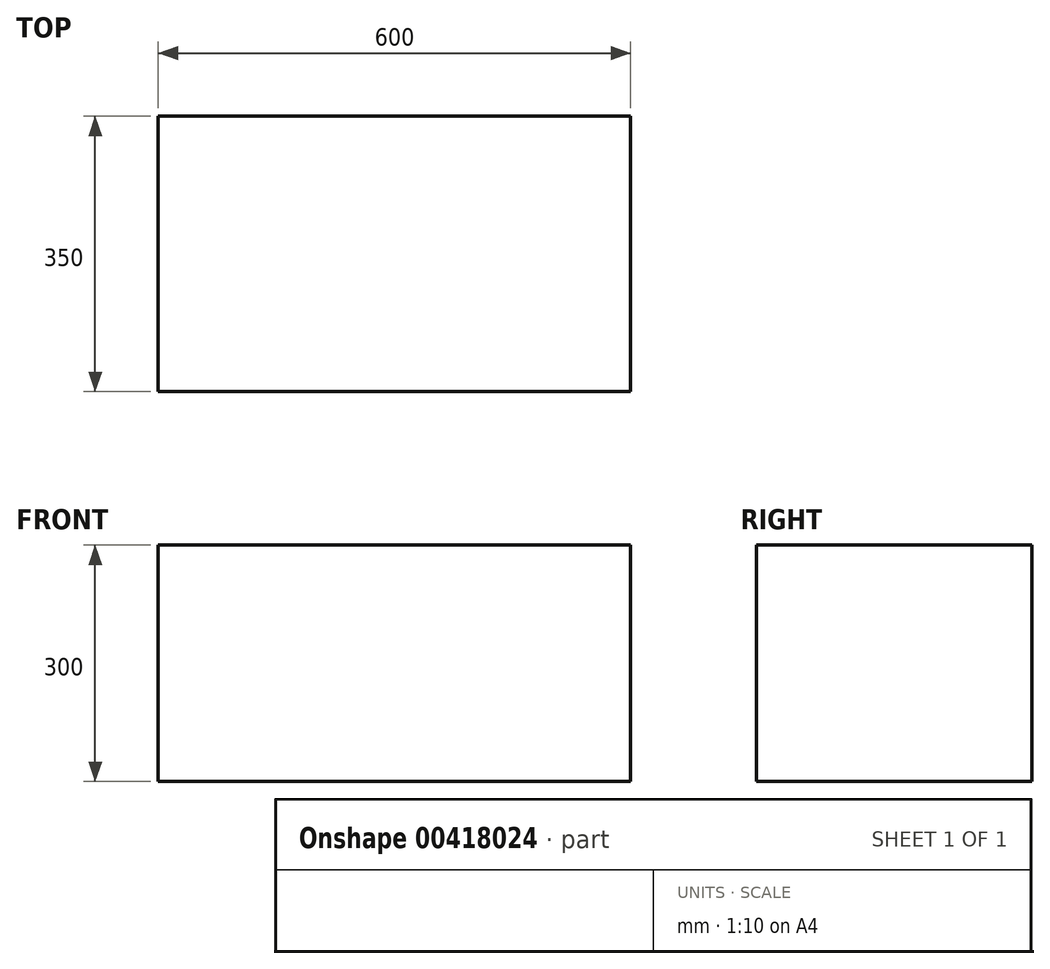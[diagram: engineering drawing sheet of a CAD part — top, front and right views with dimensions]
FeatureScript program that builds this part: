
annotation { "Feature Type Name" : "Feature", "Feature Type Description" : "" }
export const myFeature = defineFeature(function(context is Context, id is Id, definition is map)
    precondition{}
    {
        {
            var Q0;
            Q0=qCreatedBy(makeId("Front.planeOp"),FACE);
            var sketch = newSketch(context, id + "F0", { "sketchPlane" : qUnion([Q0])});
            skLineSegment(sketch, "E0.bottom", {"start": v(300, -150) * mm, "end": v(-300, -150) * mm});
            skLineSegment(sketch, "E0.top", {"start": v(300, 150) * mm, "end": v(-300, 150) * mm});
            skLineSegment(sketch, "E0.left", {"start": v(300, -150) * mm, "end": v(300, 150) * mm});
            skLineSegment(sketch, "E0.right", {"start": v(-300, -150) * mm, "end": v(-300, 150) * mm});
            skPoint(sketch, "E0.middle", {"position": v(0, 0) * mm});
            skSolve(sketch);
        }
        {
            var Q0;
            Q0=makeQuery(id+"F0.imprint","IMPRINT",FACE,{"disambiguationData":[TD([[makeQuery(id+"F0.imprint","IMPRINT",EDGE,{"derivedFrom":sQuery(id+"F0.wireOp",EDGE,"E0.bottom")}),-1.0]])]});
            extrude(context, id + "F1", {"entities" : qUnion([Q0]), "depth" : 350 * mm});
        }
    });
